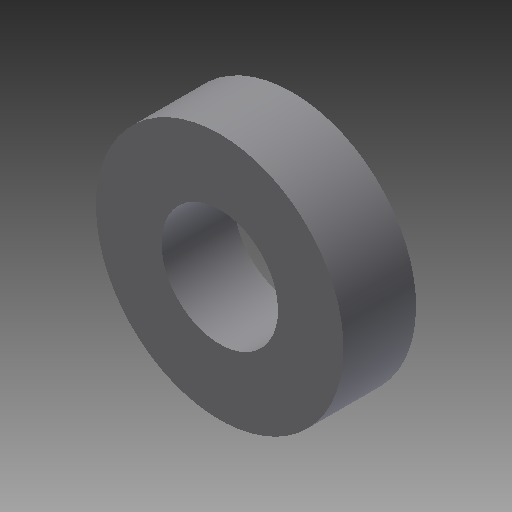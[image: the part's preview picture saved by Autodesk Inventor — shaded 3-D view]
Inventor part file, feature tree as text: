
AUTODESK INVENTOR PART (.ipt)
format: ipt  version: 2019.4 (Build 234330000, 330)  size: 108,032 bytes
history: native  units: in
note: dims shown in document units (in); Inventor stores cm internally (conversion verified against a paired STEP export)
features: other x7, revolve x1, sketch x1
ambient origin geometry x8: Origin, YZ Plane, XZ Plane, XY Plane, X Axis, Y Axis, Z Axis, Center Point
bodies: Solid1 (feature_tree)
feature tree (9):
  revolve  "Revolution1"  [1 undecoded]
  other  "part_to_rod_XY"
  other  "part_to_rod_YZ"
  other  "part_to_rod_ZX"
  other  "part_to_rod_X"
  other  "part_to_rod_Y"
  other  "part_to_rod_Z"
  other  "part_to_rod_Center"
  sketch  "Sketch_1"  dims[d0=360.0deg]
note: 1 required parameter value undecoded (feature->parameter linkage not recoverable at this tier; creation-order binding heuristic only, values carry confidence <= 0.55)
